# Revit family: result
name_source: partatom
category: Furniture
revit_build: Autodesk Revit 2015 (Build: 20140903_1530(x64)
units: mm (PartAtom-declared; Revit-internal decimal feet)

## types (1)
- Default
    BIMobject category = Hooks & Hangers
    BIMobject category code = furniture-hooks-hangers
    BIMobject main category = Furniture
    BIMobject main category code = furniture
    Brand url = http://www.hansgrohe-int.com
    Design country = Germany
    Edition number = 1
    GTIN code = https://4059625203446
    IFC Classification = Furnishing Element
    Installation instructions = https://www.hansgrohe-usa.com
    Manufacturer country = Germany
    Manufacturer name = hansgrohe
    Masterformat 2014 Code = 41 23 19
    Masterformat 2014 Description = Hooks
    NBS Reference Code = 36-59-38
    NBS Reference Description = Holders And Hooks
    OmniClass Code = 23-31 25 25
    OmniClass Description = Towel Bars
    Product Guid = 4932f9b1-3710-43ce-bd8b-bfe3047c8b55
    Product SKU = 04785820
    Product data url = https://bimobject.com
    Product family = Joleena
    Product group = Towel holder
    Product name = 04785820 Joleena Bath towel rail 24"
    Product url = https://www.hansgrohe-usa.com
    QR code = http://bimobject.com
    Technical description = https://www.hansgrohe-usa.com
    UNSPSC Code = 56
    Uniclass 1.4 Code = JN
    Uniclass 1.4 Description = Furniture/Equipment
    Uniclass 2.0 Code = PR-36-59-38
    Uniclass 2.0 Description = Holders And Hooks
    Uniclass 2015 Code = Pr_30_36_59_38
    Uniclass 2015 Name = Holders and hooks
    Uniformat II Code = E1090
    Uniformat II Description = Other Equipment

## geometry (parser evidence)
native form markers: Sweep x4
no freeform markers — native parametric forms only
